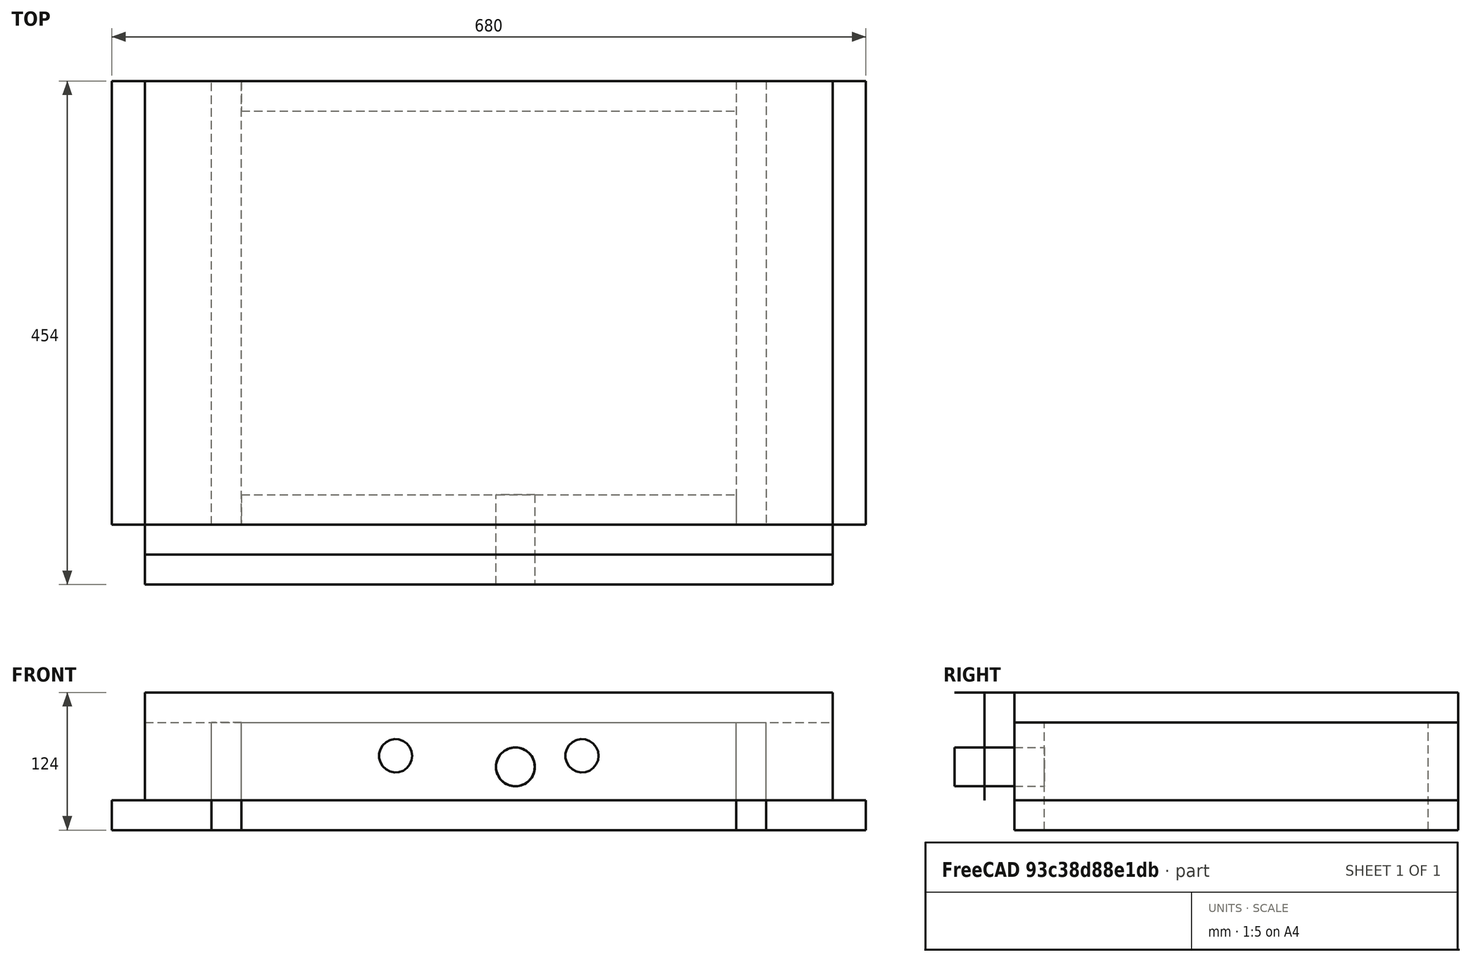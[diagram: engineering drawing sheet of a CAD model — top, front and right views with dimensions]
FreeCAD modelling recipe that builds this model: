
FCSTD DOCUMENT  (FreeCAD 0.20R25131 (Git))
Label: Werkbank
License: All rights reserved
LicenseURL: http://en.wikipedia.org/wiki/All_rights_reserved
objects: App::FeaturePython×76, Part::FeaturePython×42, App::Link×6, App::LinkElement×6
note: 41 computed .brp shape members not serialized (recipe doc carries the construction recipe); baked Part::Feature solids carry a one-line shape summary decoded from their .brp
EXTERNAL_REF file=Arbeitsfläche.FCStd obj=Assembly
EXTERNAL_REF file=Innen_hinten.FCStd obj=Assembly
EXTERNAL_REF file=Innen_vorne.FCStd obj=Assembly
EXTERNAL_REF file=Seitenteil.FCStd obj=Assembly
EXTERNAL_REF file=Grunddaten.FCStd obj=Spreadsheet
EXTERNAL_REF file=Zange.FCStd obj=Assembly
EXTERNAL_REF file=Klemmfläche.FCStd obj=Assembly

FEATURE [App::Link] Link  label="Arbeitsfläche"
  LinkedObject = -> <external Arbeitsfläche.FCStd>#Assembly
FEATURE [App::Link] Link001  label="Innen_hinten"
  LinkPlacement = pos=(87,400,-97) rot=(1,0,0;1.5708rad)
  LinkedObject = -> <external Innen_hinten.FCStd>#Assembly
  Placement = pos=(87,400,-97) rot=(1,0,0;1.5708rad)
FEATURE [App::Link] Link002  label="Innen_vorne"
  LinkPlacement = pos=(310,27,-97) rot=(1,0,0;1.5708rad)
  LinkedObject = -> <external Innen_vorne.FCStd>#Assembly
  Placement = pos=(310,27,-97) rot=(1,0,0;1.5708rad)
FEATURE [App::LinkElement] Link003_i0
  LinkPlacement = pos=(87,-4.17804e-09,-97) rot=(0,-1,0;1.5708rad)
  LinkedObject = -> <external Seitenteil.FCStd>#Assembly
  Placement = pos=(87,-4.17804e-09,-97) rot=(0,-1,0;1.5708rad)
FEATURE [App::LinkElement] Link003_i1
  LinkPlacement = pos=(533,400,-97) rot=(0.707107,0,0.707107;3.14159rad)
  LinkedObject = -> <external Seitenteil.FCStd>#Assembly
  Placement = pos=(533,400,-97) rot=(0.707107,0,0.707107;3.14159rad)
FEATURE [App::Link] Link003  label="Seitenteil"
  ElementCount = 2
  ElementList = -> [Link003_i0,Link003_i1]
  LinkedObject = -> <external Seitenteil.FCStd>#Assembly
FEATURE [App::LinkElement] Link004_i0
  LinkPlacement = pos=(310,1.40084e-11,-70) rot=(1,0,0;1.5708rad)
  LinkedObject = -> <external Zange.FCStd>#Assembly
  Placement = pos=(310,1.40084e-11,-70) rot=(1,0,0;1.5708rad)
FEATURE [App::LinkElement] Link004_i1
  LinkPlacement = pos=(310,-27,-70) rot=(1,0,0;1.5708rad)
  LinkedObject = -> <external Zange.FCStd>#Assembly
  Placement = pos=(310,-27,-70) rot=(1,0,0;1.5708rad)
FEATURE [App::Link] Link004  label="Zange"
  ElementCount = 2
  ElementList = -> [Link004_i0,Link004_i1]
  LinkedObject = -> <external Zange.FCStd>#Assembly
FEATURE [App::LinkElement] Link005_i0
  LinkPlacement = pos=(-30,9.2e-15,-97) rot=(0,0,1;0rad)
  LinkedObject = -> <external Klemmfläche.FCStd>#Assembly
  Placement = pos=(-30,9.2e-15,-97) rot=(0,0,1;0rad)
FEATURE [App::LinkElement] Link005_i1
  LinkPlacement = pos=(560,3.808e-13,-97) rot=(0,0,1;0rad)
  LinkedObject = -> <external Klemmfläche.FCStd>#Assembly
  Placement = pos=(560,3.808e-13,-97) rot=(0,0,1;0rad)
FEATURE [App::Link] Link005  label="Klemmfläche"
  ElementCount = 2
  ElementList = -> [Link005_i0,Link005_i1]
  LinkedObject = -> <external Klemmfläche.FCStd>#Assembly
FEATURE [Part::FeaturePython] Parts  # WARN: FeaturePython — macro-defined, semantics opaque (R4)
  Group = -> [Link,Link001,Link002,Link003,Link004,Link005]
  GroupMode = 0
FEATURE [Part::FeaturePython] Assembly  # WARN: FeaturePython — macro-defined, semantics opaque (R4)
  AutoRelax = true
  BuildShape = 0
  Freeze = false
  Group = -> [Constraints,Elements,Parts]
  Verbose = false
  _SolverType = 1
  _Version = 1
FEATURE [App::FeaturePython] Constraints  # WARN: FeaturePython — macro-defined, semantics opaque (R4)
  Group = -> [Constraint,Constraint001,Constraint002,Constraint003,Constraint004,Constraint005,Constraint006,Constraint007,Constraint008,Constraint009,Constraint010,Constraint013,Constraint014,Constraint015,Constraint016,Constraint017,Constraint018,Constraint019,Constraint020,Constraint021,Constraint022,Constraint023,Constraint024,Constraint025,Constraint026]
  _Version = 1
FEATURE [App::FeaturePython] Elements  # WARN: FeaturePython — macro-defined, semantics opaque (R4)
  Group = -> [_Element,_Element001,_Element002,_Element003,_Element004,_Element005,_Element006,_Element007,_Element008,_Element009,_Element010,_Element012,_Element013,_Element014,_Element015,_Element016,_Element017,_Element020,_Element022,_Element023,_Element024,_Element027,_Element028,_Element029,_Element030,_Element031,_Element032,_Element033,_Element034,_Element035,_Element036,_Element037,_Element038,+7 more]
FEATURE [App::FeaturePython] Constraint  label="Locked"  # WARN: FeaturePython — macro-defined, semantics opaque (R4)
  Disabled = false
  Group = -> [ElementLink]
  _ConstraintType = 0
  _Parent = -> Constraints
FEATURE [App::FeaturePython] ElementLink  label="Unten@Arbeitsfläche"  # link proxy (typed FeaturePython)
  LinkTransform = true
  LinkedObject = -> _Element
  _Parent = -> Constraint
FEATURE [Part::FeaturePython] _Element  label="Unten@Arbeitsfläche"  # link proxy (typed FeaturePython)
  Detach = false
  LinkTransform = true
  LinkedObject = -> Link [1.$Unten.]
  _Parent = -> Elements
FEATURE [Part::FeaturePython] _Element001  label="Oben@Innen_hinten"  # link proxy (typed FeaturePython)
  Detach = false
  LinkTransform = true
  LinkedObject = -> Link001 [1.$Oben.]
  _Parent = -> Elements
FEATURE [App::FeaturePython] Constraint001  label="PlaneAlignment"  # WARN: FeaturePython — macro-defined, semantics opaque (R4)
  Angle = 0
  AnglePitch = 0
  AngleRoll = 0
  Cascade = false
  Disabled = false
  Group = -> [ElementLink001,ElementLink002]
  LockAngle = false
  _ConstraintType = 37
  _Parent = -> Constraints
FEATURE [App::FeaturePython] ElementLink001  label="Oben@Innen_hinten"  # link proxy (typed FeaturePython)
  LinkTransform = true
  LinkedObject = -> _Element001
  _Parent = -> Constraint001
FEATURE [App::FeaturePython] ElementLink002  label="Unten@Arbeitsfläche"  # link proxy (typed FeaturePython)
  LinkTransform = true
  LinkedObject = -> _Element
  _Parent = -> Constraint001
FEATURE [App::FeaturePython] Constraint002  label="PlaneAlignment001"  # WARN: FeaturePython — macro-defined, semantics opaque (R4)
  Angle = 0
  AnglePitch = 0
  AngleRoll = 0
  Cascade = false
  Disabled = false
  Group = -> [ElementLink003,ElementLink004]
  LockAngle = false
  _ConstraintType = 37
  _Parent = -> Constraints
FEATURE [App::FeaturePython] ElementLink003  label="Hinten@Arbeitsfläche"  # link proxy (typed FeaturePython)
  LinkTransform = true
  LinkedObject = -> _Element002
  _Parent = -> Constraint002
FEATURE [Part::FeaturePython] _Element002  label="Hinten@Arbeitsfläche"  # link proxy (typed FeaturePython)
  Detach = false
  LinkTransform = true
  LinkedObject = -> Link [1.$Hinten.]
  _Parent = -> Elements
FEATURE [App::FeaturePython] ElementLink004  label="Hinten@Innen_hinten"  # link proxy (typed FeaturePython)
  LinkTransform = true
  LinkedObject = -> _Element003
  _Parent = -> Constraint002
FEATURE [Part::FeaturePython] _Element003  label="Hinten@Innen_hinten"  # link proxy (typed FeaturePython)
  Detach = false
  LinkTransform = true
  LinkedObject = -> Link001 [1.$Hinten.]
  _Parent = -> Elements
FEATURE [App::FeaturePython] Constraint003  label="PlaneAlignment002"  # WARN: FeaturePython — macro-defined, semantics opaque (R4)
  Angle = 0
  AnglePitch = 0
  AngleRoll = 0
  Cascade = false
  Disabled = false
  Group = -> [ElementLink005,ElementLink006]
  LockAngle = false
  _ConstraintType = 37
  _Parent = -> Constraints
FEATURE [App::FeaturePython] ElementLink005  label="Oben@Innen_vorne"  # link proxy (typed FeaturePython)
  LinkTransform = true
  LinkedObject = -> _Element004
  _Parent = -> Constraint003
FEATURE [Part::FeaturePython] _Element004  label="Oben@Innen_vorne"  # link proxy (typed FeaturePython)
  Detach = false
  LinkTransform = true
  LinkedObject = -> Link002 [1.$Oben.]
  _Parent = -> Elements
FEATURE [App::FeaturePython] ElementLink006  label="Unten@Arbeitsfläche"  # link proxy (typed FeaturePython)
  LinkTransform = true
  LinkedObject = -> _Element
  _Parent = -> Constraint003
FEATURE [App::FeaturePython] Constraint004  label="PlaneAlignment003"  # WARN: FeaturePython — macro-defined, semantics opaque (R4)
  Angle = 0
  AnglePitch = 0
  AngleRoll = 0
  Cascade = false
  Disabled = false
  Group = -> [ElementLink007,ElementLink008]
  LockAngle = false
  _ConstraintType = 37
  _Parent = -> Constraints
FEATURE [App::FeaturePython] ElementLink007  label="Vorne@Innen_vorne"  # link proxy (typed FeaturePython)
  LinkTransform = true
  LinkedObject = -> _Element005
  _Parent = -> Constraint004
FEATURE [Part::FeaturePython] _Element005  label="Vorne@Innen_vorne"  # link proxy (typed FeaturePython)
  Detach = false
  LinkTransform = true
  LinkedObject = -> Link002 [1.$Vorne.]
  _Parent = -> Elements
FEATURE [App::FeaturePython] ElementLink008  label="Vorne@Arbeitsfläche"  # link proxy (typed FeaturePython)
  LinkTransform = true
  LinkedObject = -> _Element006
  _Parent = -> Constraint004
FEATURE [Part::FeaturePython] _Element006  label="Vorne@Arbeitsfläche"  # link proxy (typed FeaturePython)
  Detach = false
  LinkTransform = true
  LinkedObject = -> Link [1.$Vorne.]
  _Parent = -> Elements
FEATURE [App::FeaturePython] Constraint005  label="PlaneAlignment004"  # WARN: FeaturePython — macro-defined, semantics opaque (R4)
  Angle = 0
  AnglePitch = 0
  AngleRoll = 0
  Cascade = false
  Disabled = false
  Group = -> [ElementLink009,ElementLink010]
  LockAngle = false
  _ConstraintType = 37
  _Parent = -> Constraints
FEATURE [App::FeaturePython] ElementLink009  label="_Element007"  # link proxy (typed FeaturePython)
  LinkTransform = true
  LinkedObject = -> _Element007
  _Parent = -> Constraint005
FEATURE [Part::FeaturePython] _Element007  # link proxy (typed FeaturePython)
  Detach = false
  LinkTransform = true
  LinkedObject = -> Link003 [Link003_i0.1.$Vorne.]
  _Parent = -> Elements
FEATURE [App::FeaturePython] ElementLink010  label="Vorne@Arbeitsfläche"  # link proxy (typed FeaturePython)
  LinkTransform = true
  LinkedObject = -> _Element006
  _Parent = -> Constraint005
FEATURE [App::FeaturePython] Constraint006  label="PlaneAlignment005"  # WARN: FeaturePython — macro-defined, semantics opaque (R4)
  Angle = 0
  AnglePitch = 0
  AngleRoll = 0
  Cascade = false
  Disabled = false
  Group = -> [ElementLink011,ElementLink012]
  LockAngle = false
  _ConstraintType = 37
  _Parent = -> Constraints
FEATURE [App::FeaturePython] ElementLink011  label="_Element008"  # link proxy (typed FeaturePython)
  LinkTransform = true
  LinkedObject = -> _Element008
  _Parent = -> Constraint006
FEATURE [Part::FeaturePython] _Element008  # link proxy (typed FeaturePython)
  Detach = false
  LinkTransform = true
  LinkedObject = -> Link003 [Link003_i0.1.$Oben.]
  _Parent = -> Elements
FEATURE [App::FeaturePython] ElementLink012  label="Unten@Arbeitsfläche"  # link proxy (typed FeaturePython)
  LinkTransform = true
  LinkedObject = -> _Element
  _Parent = -> Constraint006
FEATURE [App::FeaturePython] Constraint007  label="PlaneAlignment006"  # WARN: FeaturePython — macro-defined, semantics opaque (R4)
  Angle = 0
  AnglePitch = 0
  AngleRoll = 0
  Cascade = false
  Disabled = false
  Group = -> [ElementLink013,ElementLink014]
  LockAngle = false
  Offset = 60
  _ConstraintType = 37
  _Parent = -> Constraints
  expr: Offset = Grunddaten#Spreadsheet.Ueberstand
FEATURE [App::FeaturePython] ElementLink013  label="_Element009"  # link proxy (typed FeaturePython)
  LinkTransform = true
  LinkedObject = -> _Element009
  _Parent = -> Constraint007
FEATURE [Part::FeaturePython] _Element009  # link proxy (typed FeaturePython)
  Detach = false
  LinkTransform = true
  LinkedObject = -> Link003 [Link003_i0.1.$Seite.]
  _Parent = -> Elements
FEATURE [App::FeaturePython] ElementLink014  label="Links@Arbeitsfläche"  # link proxy (typed FeaturePython)
  LinkTransform = true
  LinkedObject = -> _Element010
  _Parent = -> Constraint007
FEATURE [Part::FeaturePython] _Element010  label="Links@Arbeitsfläche"  # link proxy (typed FeaturePython)
  Detach = false
  LinkTransform = true
  LinkedObject = -> Link [1.$Links.]
  _Parent = -> Elements
FEATURE [Part::FeaturePython] _Element012  label="Rechts@Arbeitsfläche"  # link proxy (typed FeaturePython)
  Detach = false
  LinkTransform = true
  LinkedObject = -> Link [1.$Rechts.]
  _Parent = -> Elements
FEATURE [Part::FeaturePython] _Element013  # link proxy (typed FeaturePython)
  Detach = false
  LinkTransform = true
  LinkedObject = -> Link004 [Link004_i0.1.$Oben.]
  _Parent = -> Elements
FEATURE [Part::FeaturePython] _Element014  label="Oben@Arbeitsfläche"  # link proxy (typed FeaturePython)
  Detach = false
  LinkTransform = true
  LinkedObject = -> Link [1.$Oben.]
  _Parent = -> Elements
FEATURE [App::FeaturePython] Constraint008  label="PlaneAlignment007"  # WARN: FeaturePython — macro-defined, semantics opaque (R4)
  Angle = 0
  AnglePitch = 0
  AngleRoll = 0
  Cascade = false
  Disabled = false
  Group = -> [ElementLink015,ElementLink016]
  LockAngle = false
  _ConstraintType = 37
  _Parent = -> Constraints
FEATURE [App::FeaturePython] ElementLink015  label="Unten@Arbeitsfläche"  # link proxy (typed FeaturePython)
  LinkTransform = true
  LinkedObject = -> _Element
  _Parent = -> Constraint008
FEATURE [App::FeaturePython] ElementLink016  label="_Element015"  # link proxy (typed FeaturePython)
  LinkTransform = true
  LinkedObject = -> _Element015
  _Parent = -> Constraint008
FEATURE [Part::FeaturePython] _Element015  # link proxy (typed FeaturePython)
  Detach = false
  LinkTransform = true
  LinkedObject = -> Link003 [Link003_i1.1.$Oben.]
  _Parent = -> Elements
FEATURE [App::FeaturePython] Constraint009  label="PlaneAlignment008"  # WARN: FeaturePython — macro-defined, semantics opaque (R4)
  Angle = 0
  AnglePitch = 0
  AngleRoll = 0
  Cascade = false
  Disabled = false
  Group = -> [ElementLink017,ElementLink018]
  LockAngle = false
  _ConstraintType = 37
  _Parent = -> Constraints
FEATURE [App::FeaturePython] ElementLink017  label="Hinten@Arbeitsfläche"  # link proxy (typed FeaturePython)
  LinkTransform = true
  LinkedObject = -> _Element002
  _Parent = -> Constraint009
FEATURE [App::FeaturePython] ElementLink018  label="_Element016"  # link proxy (typed FeaturePython)
  LinkTransform = true
  LinkedObject = -> _Element016
  _Parent = -> Constraint009
FEATURE [Part::FeaturePython] _Element016  # link proxy (typed FeaturePython)
  Detach = false
  LinkTransform = true
  LinkedObject = -> Link003 [Link003_i1.1.$Vorne.]
  _Parent = -> Elements
FEATURE [App::FeaturePython] Constraint010  label="PlaneAlignment009"  # WARN: FeaturePython — macro-defined, semantics opaque (R4)
  Angle = 0
  AnglePitch = 0
  AngleRoll = 0
  Cascade = false
  Disabled = false
  Group = -> [ElementLink019,ElementLink020]
  LockAngle = false
  Offset = 60
  _ConstraintType = 37
  _Parent = -> Constraints
  expr: Offset = Grunddaten#Spreadsheet.Ueberstand
FEATURE [App::FeaturePython] ElementLink019  label="_Element017"  # link proxy (typed FeaturePython)
  LinkTransform = true
  LinkedObject = -> _Element017
  _Parent = -> Constraint010
FEATURE [Part::FeaturePython] _Element017  # link proxy (typed FeaturePython)
  Detach = false
  LinkTransform = true
  LinkedObject = -> Link003 [Link003_i1.1.$Seite.]
  _Parent = -> Elements
FEATURE [App::FeaturePython] ElementLink020  label="Rechts@Arbeitsfläche"  # link proxy (typed FeaturePython)
  LinkTransform = true
  LinkedObject = -> _Element012
  _Parent = -> Constraint010
FEATURE [Part::FeaturePython] _Element020  # link proxy (typed FeaturePython)
  Detach = false
  LinkTransform = true
  LinkedObject = -> Link004 [1.1.$Spindel.]
  _Parent = -> Elements
FEATURE [Part::FeaturePython] _Element022  # link proxy (typed FeaturePython)
  Detach = false
  LinkTransform = true
  LinkedObject = -> Link004 [0.1.$Spindel.]
  _Parent = -> Elements
FEATURE [Part::FeaturePython] _Element023  # link proxy (typed FeaturePython)
  Detach = false
  LinkTransform = true
  LinkedObject = -> Link002 [1.$Element003.]
  _Parent = -> Elements
FEATURE [App::FeaturePython] Constraint013  label="PlaneAlignment010"  # WARN: FeaturePython — macro-defined, semantics opaque (R4)
  Angle = 0
  AnglePitch = 0
  AngleRoll = 0
  Cascade = false
  Disabled = false
  Group = -> [ElementLink025,ElementLink026]
  LockAngle = false
  _ConstraintType = 37
  _Parent = -> Constraints
FEATURE [App::FeaturePython] ElementLink025  label="_Element024"  # link proxy (typed FeaturePython)
  LinkTransform = true
  LinkedObject = -> _Element024
  _Parent = -> Constraint013
FEATURE [Part::FeaturePython] _Element024  # link proxy (typed FeaturePython)
  Detach = false
  LinkTransform = true
  LinkedObject = -> Link004 [Link004_i0.1.$Hinten.]
  _Parent = -> Elements
FEATURE [App::FeaturePython] ElementLink026  label="Vorne@Arbeitsfläche"  # link proxy (typed FeaturePython)
  LinkTransform = true
  LinkedObject = -> _Element006
  _Parent = -> Constraint013
FEATURE [App::FeaturePython] Constraint014  label="PlaneAlignment011"  # WARN: FeaturePython — macro-defined, semantics opaque (R4)
  Angle = 0
  AnglePitch = 0
  AngleRoll = 0
  Cascade = false
  Disabled = false
  Group = -> [ElementLink027,ElementLink028]
  LockAngle = false
  _ConstraintType = 37
  _Parent = -> Constraints
FEATURE [App::FeaturePython] ElementLink027  label="_Element013"  # link proxy (typed FeaturePython)
  LinkTransform = true
  LinkedObject = -> _Element013
  _Parent = -> Constraint014
FEATURE [App::FeaturePython] ElementLink028  label="Oben@Arbeitsfläche"  # link proxy (typed FeaturePython)
  LinkTransform = true
  LinkedObject = -> _Element014
  _Parent = -> Constraint014
FEATURE [Part::FeaturePython] _Element027  # link proxy (typed FeaturePython)
  Detach = false
  LinkTransform = true
  LinkedObject = -> Link004 [Link004_i0.1.$Vorne.]
  _Parent = -> Elements
FEATURE [App::FeaturePython] Constraint015  label="PlaneAlignment012"  # WARN: FeaturePython — macro-defined, semantics opaque (R4)
  Angle = 0
  AnglePitch = 0
  AngleRoll = 0
  Cascade = false
  Disabled = false
  Group = -> [ElementLink029,ElementLink030]
  LockAngle = false
  _ConstraintType = 37
  _Parent = -> Constraints
FEATURE [App::FeaturePython] ElementLink029  label="_Element028"  # link proxy (typed FeaturePython)
  LinkTransform = true
  LinkedObject = -> _Element028
  _Parent = -> Constraint015
FEATURE [Part::FeaturePython] _Element028  # link proxy (typed FeaturePython)
  Detach = false
  LinkTransform = true
  LinkedObject = -> Link002 [1.$Element004.]
  _Parent = -> Elements
FEATURE [App::FeaturePython] ElementLink030  label="_Element029"  # link proxy (typed FeaturePython)
  LinkTransform = true
  LinkedObject = -> _Element029
  _Parent = -> Constraint015
FEATURE [Part::FeaturePython] _Element029  # link proxy (typed FeaturePython)
  Detach = false
  LinkTransform = true
  LinkedObject = -> Link003 [0.1.$Element003.]
  _Parent = -> Elements
FEATURE [App::FeaturePython] Constraint016  label="PlaneAlignment013"  # WARN: FeaturePython — macro-defined, semantics opaque (R4)
  Angle = 0
  AnglePitch = 0
  AngleRoll = 0
  Cascade = false
  Disabled = false
  Group = -> [ElementLink031,ElementLink032]
  LockAngle = false
  _ConstraintType = 37
  _Parent = -> Constraints
FEATURE [App::FeaturePython] ElementLink031  label="_Element030"  # link proxy (typed FeaturePython)
  LinkTransform = true
  LinkedObject = -> _Element030
  _Parent = -> Constraint016
FEATURE [Part::FeaturePython] _Element030  # link proxy (typed FeaturePython)
  Detach = false
  LinkTransform = true
  LinkedObject = -> Link001 [1.$Element002.]
  _Parent = -> Elements
FEATURE [App::FeaturePython] ElementLink032  label="_Element029"  # link proxy (typed FeaturePython)
  LinkTransform = true
  LinkedObject = -> _Element029
  _Parent = -> Constraint016
FEATURE [App::FeaturePython] Constraint017  label="AxialAlignment"  # WARN: FeaturePython — macro-defined, semantics opaque (R4)
  Angle = 0
  AnglePitch = 0
  AngleRoll = 0
  Disabled = false
  Group = -> [ElementLink033,ElementLink034]
  LockAngle = false
  Multiply = false
  _ConstraintType = 36
  _Parent = -> Constraints
FEATURE [App::FeaturePython] ElementLink033  label="_Element031"  # link proxy (typed FeaturePython)
  LinkTransform = true
  LinkedObject = -> _Element031
  _Parent = -> Constraint017
FEATURE [Part::FeaturePython] _Element031  # link proxy (typed FeaturePython)
  Detach = false
  LinkTransform = true
  LinkedObject = -> Link004 [Link004_i0.1.$Spindel.]
  _Parent = -> Elements
FEATURE [App::FeaturePython] ElementLink034  label="Spindel@Innen_vorne"  # link proxy (typed FeaturePython)
  LinkTransform = true
  LinkedObject = -> _Element032
  _Parent = -> Constraint017
FEATURE [Part::FeaturePython] _Element032  label="Spindel@Innen_vorne"  # link proxy (typed FeaturePython)
  Detach = false
  LinkTransform = true
  LinkedObject = -> Link002 [1.$Spindel.]
  _Parent = -> Elements
FEATURE [App::FeaturePython] Constraint018  label="AxialAlignment001"  # WARN: FeaturePython — macro-defined, semantics opaque (R4)
  Angle = 0
  AnglePitch = 0
  AngleRoll = 0
  Disabled = false
  Group = -> [ElementLink035,ElementLink036]
  LockAngle = false
  Multiply = false
  _ConstraintType = 36
  _Parent = -> Constraints
FEATURE [App::FeaturePython] ElementLink035  label="_Element033"  # link proxy (typed FeaturePython)
  LinkTransform = true
  LinkedObject = -> _Element033
  _Parent = -> Constraint018
FEATURE [Part::FeaturePython] _Element033  # link proxy (typed FeaturePython)
  Detach = false
  LinkTransform = true
  LinkedObject = -> Link004 [Link004_i1.1.$Spindel.]
  _Parent = -> Elements
FEATURE [App::FeaturePython] ElementLink036  label="_Element031"  # link proxy (typed FeaturePython)
  LinkTransform = true
  LinkedObject = -> _Element031
  _Parent = -> Constraint018
FEATURE [App::FeaturePython] Constraint019  label="PlaneAlignment014"  # WARN: FeaturePython — macro-defined, semantics opaque (R4)
  Angle = 0
  AnglePitch = 0
  AngleRoll = 0
  Cascade = false
  Disabled = false
  Group = -> [ElementLink037,ElementLink038]
  LockAngle = false
  _ConstraintType = 37
  _Parent = -> Constraints
FEATURE [App::FeaturePython] ElementLink037  label="_Element013"  # link proxy (typed FeaturePython)
  LinkTransform = true
  LinkedObject = -> _Element013
  _Parent = -> Constraint019
FEATURE [App::FeaturePython] ElementLink038  label="_Element034"  # link proxy (typed FeaturePython)
  LinkTransform = true
  LinkedObject = -> _Element034
  _Parent = -> Constraint019
FEATURE [Part::FeaturePython] _Element034  # link proxy (typed FeaturePython)
  Detach = false
  LinkTransform = true
  LinkedObject = -> Link004 [Link004_i1.1.$Oben.]
  _Parent = -> Elements
FEATURE [App::FeaturePython] Constraint020  label="PlaneAlignment015"  # WARN: FeaturePython — macro-defined, semantics opaque (R4)
  Angle = 0
  AnglePitch = 0
  AngleRoll = 0
  Cascade = false
  Disabled = false
  Group = -> [ElementLink039,ElementLink040]
  LockAngle = false
  _ConstraintType = 37
  _Parent = -> Constraints
FEATURE [App::FeaturePython] ElementLink039  label="_Element007"  # link proxy (typed FeaturePython)
  LinkTransform = true
  LinkedObject = -> _Element007
  _Parent = -> Constraint020
FEATURE [App::FeaturePython] ElementLink040  label="_Element035"  # link proxy (typed FeaturePython)
  LinkTransform = true
  LinkedObject = -> _Element035
  _Parent = -> Constraint020
FEATURE [Part::FeaturePython] _Element035  # link proxy (typed FeaturePython)
  Detach = false
  LinkTransform = true
  LinkedObject = -> Link005 [Link005_i0.1.$Vorne.]
  _Parent = -> Elements
FEATURE [App::FeaturePython] Constraint021  label="PlaneAlignment016"  # WARN: FeaturePython — macro-defined, semantics opaque (R4)
  Angle = 0
  AnglePitch = 0
  AngleRoll = 0
  Cascade = false
  Disabled = false
  Group = -> [ElementLink041,ElementLink042]
  LockAngle = false
  _ConstraintType = 37
  _Parent = -> Constraints
FEATURE [App::FeaturePython] ElementLink041  label="_Element036"  # link proxy (typed FeaturePython)
  LinkTransform = true
  LinkedObject = -> _Element036
  _Parent = -> Constraint021
FEATURE [Part::FeaturePython] _Element036  # link proxy (typed FeaturePython)
  Detach = false
  LinkTransform = true
  LinkedObject = -> Link005 [Link005_i0.1.$Rechts.]
  _Parent = -> Elements
FEATURE [App::FeaturePython] ElementLink042  label="_Element009"  # link proxy (typed FeaturePython)
  LinkTransform = true
  LinkedObject = -> _Element009
  _Parent = -> Constraint021
FEATURE [App::FeaturePython] Constraint022  label="PlaneAlignment017"  # WARN: FeaturePython — macro-defined, semantics opaque (R4)
  Angle = 0
  AnglePitch = 0
  AngleRoll = 0
  Cascade = false
  Disabled = false
  Group = -> [ElementLink043,ElementLink044]
  LockAngle = false
  _ConstraintType = 37
  _Parent = -> Constraints
FEATURE [App::FeaturePython] ElementLink043  label="_Element037"  # link proxy (typed FeaturePython)
  LinkTransform = true
  LinkedObject = -> _Element037
  _Parent = -> Constraint022
FEATURE [Part::FeaturePython] _Element037  # link proxy (typed FeaturePython)
  Detach = false
  LinkTransform = true
  LinkedObject = -> Link005 [Link005_i1.1.$Vorne.]
  _Parent = -> Elements
FEATURE [App::FeaturePython] ElementLink044  label="_Element007"  # link proxy (typed FeaturePython)
  LinkTransform = true
  LinkedObject = -> _Element007
  _Parent = -> Constraint022
FEATURE [Part::FeaturePython] _Element038  # link proxy (typed FeaturePython)
  Detach = false
  LinkTransform = true
  LinkedObject = -> Link005 [Link005_i0.1.$Links.]
  _Parent = -> Elements
FEATURE [App::FeaturePython] Constraint023  label="PlaneAlignment018"  # WARN: FeaturePython — macro-defined, semantics opaque (R4)
  Angle = 0
  AnglePitch = 0
  AngleRoll = 0
  Cascade = false
  Disabled = false
  Group = -> [ElementLink045,ElementLink046]
  LockAngle = false
  _ConstraintType = 37
  _Parent = -> Constraints
FEATURE [App::FeaturePython] ElementLink045  label="_Element039"  # link proxy (typed FeaturePython)
  LinkTransform = true
  LinkedObject = -> _Element039
  _Parent = -> Constraint023
FEATURE [Part::FeaturePython] _Element039  # link proxy (typed FeaturePython)
  Detach = false
  LinkTransform = true
  LinkedObject = -> Link005 [0.1.$Unten.]
  _Parent = -> Elements
FEATURE [App::FeaturePython] ElementLink046  label="_Element040"  # link proxy (typed FeaturePython)
  LinkTransform = true
  LinkedObject = -> _Element040
  _Parent = -> Constraint023
FEATURE [Part::FeaturePython] _Element040  # link proxy (typed FeaturePython)
  Detach = false
  LinkTransform = true
  LinkedObject = -> Link003 [0.1.$Element004.]
  _Parent = -> Elements
FEATURE [App::FeaturePython] Constraint024  label="PlaneAlignment019"  # WARN: FeaturePython — macro-defined, semantics opaque (R4)
  Angle = 0
  AnglePitch = 0
  AngleRoll = 0
  Cascade = false
  Disabled = false
  Group = -> [ElementLink047,ElementLink048]
  LockAngle = false
  _ConstraintType = 37
  _Parent = -> Constraints
FEATURE [App::FeaturePython] ElementLink047  label="_Element041"  # link proxy (typed FeaturePython)
  LinkTransform = true
  LinkedObject = -> _Element041
  _Parent = -> Constraint024
FEATURE [Part::FeaturePython] _Element041  # link proxy (typed FeaturePython)
  Detach = false
  LinkTransform = true
  LinkedObject = -> Link005 [Link005_i1.1.$Unten.]
  _Parent = -> Elements
FEATURE [App::FeaturePython] ElementLink048  label="_Element042"  # link proxy (typed FeaturePython)
  LinkTransform = true
  LinkedObject = -> _Element042
  _Parent = -> Constraint024
FEATURE [Part::FeaturePython] _Element042  # link proxy (typed FeaturePython)
  Detach = false
  LinkTransform = true
  LinkedObject = -> Link005 [Link005_i0.1.$Unten.]
  _Parent = -> Elements
FEATURE [App::FeaturePython] Constraint025  label="PlaneAlignment020"  # WARN: FeaturePython — macro-defined, semantics opaque (R4)
  Angle = 0
  AnglePitch = 0
  AngleRoll = 0
  Cascade = false
  Disabled = false
  Group = -> [ElementLink049,ElementLink050]
  LockAngle = false
  _ConstraintType = 37
  _Parent = -> Constraints
FEATURE [App::FeaturePython] ElementLink049  label="_Element043"  # link proxy (typed FeaturePython)
  LinkTransform = true
  LinkedObject = -> _Element043
  _Parent = -> Constraint025
FEATURE [Part::FeaturePython] _Element043  # link proxy (typed FeaturePython)
  Detach = false
  LinkTransform = true
  LinkedObject = -> Link005 [Link005_i1.1.$Links.]
  _Parent = -> Elements
FEATURE [App::FeaturePython] ElementLink050  label="_Element017"  # link proxy (typed FeaturePython)
  LinkTransform = true
  LinkedObject = -> _Element017
  _Parent = -> Constraint025
FEATURE [App::FeaturePython] Constraint026  label="PlaneAlignment021"  # WARN: FeaturePython — macro-defined, semantics opaque (R4)
  Angle = 0
  AnglePitch = 0
  AngleRoll = 0
  Cascade = false
  Disabled = false
  Group = -> [ElementLink051,ElementLink052]
  LockAngle = false
  _ConstraintType = 37
  _Parent = -> Constraints
FEATURE [App::FeaturePython] ElementLink051  label="_Element044"  # link proxy (typed FeaturePython)
  LinkTransform = true
  LinkedObject = -> _Element044
  _Parent = -> Constraint026
FEATURE [Part::FeaturePython] _Element044  # link proxy (typed FeaturePython)
  Detach = false
  LinkTransform = true
  LinkedObject = -> Link004 [1.1.$Hinten.]
  _Parent = -> Elements
FEATURE [App::FeaturePython] ElementLink052  label="_Element045"  # link proxy (typed FeaturePython)
  LinkTransform = true
  LinkedObject = -> _Element045
  _Parent = -> Constraint026
FEATURE [Part::FeaturePython] _Element045  # link proxy (typed FeaturePython)
  Detach = false
  LinkTransform = true
  LinkedObject = -> Link004 [0.1.$Vorne.]
  _Parent = -> Elements

RESOLVED EXTERNAL PARTS (link-assembly join: the EXTERNAL_REF files above that resolve inside this repo's crawl, each included once):
---- part Arbeitsfläche.FCStd = doc fcstd_90bbc381280e ----
FCSTD DOCUMENT  (FreeCAD 0.20R25131 (Git))
Label: Arbeitsfläche
License: All rights reserved
LicenseURL: http://en.wikipedia.org/wiki/All_rights_reserved
objects: Part::FeaturePython×8, App::FeaturePython×2, Part::Box×1, Part::Cylinder×1, Part::Cut×1
note: 10 computed .brp shape members not serialized (recipe doc carries the construction recipe); baked Part::Feature solids carry a one-line shape summary decoded from their .brp
EXTERNAL_REF file=Grunddaten.FCStd obj=Spreadsheet

FEATURE [Part::Box] Box  label="Cube"
  AttacherType = Attacher::AttachEngine3D
  Height = 27
  Length = 620
  Width = 400
  expr: Length = <<Grunddaten>>#Spreadsheet.Arbeitsflaeche + 2 * <<Grunddaten>>#Spreadsheet.Ueberstand
  expr: Width = <<Grunddaten>>#Spreadsheet.Plattenbreite
  expr: Height = <<Grunddaten>>#Spreadsheet.Plattendicke
FEATURE [App::FeaturePython] Constraints  # WARN: FeaturePython — macro-defined, semantics opaque (R4)
  _Version = 1
FEATURE [Part::Cylinder] Cylinder  label="Schraubzwinge_oben"
  Angle = 360
  AttacherType = Attacher::AttachEngine3D
  FirstAngle = 0
  Height = 30
  Placement = pos=(485,60,0) rot=(0,0,1;0rad)
  Radius = 25
  SecondAngle = 0
  expr: .Placement.Base.x = Grunddaten#Spreadsheet.Arbeitsflaeche + Grunddaten#Spreadsheet.Ueberstand - 75mm
FEATURE [Part::Cut] Cut
  Base = -> Box
  Tool = -> Cylinder
FEATURE [Part::FeaturePython] Parts  # WARN: FeaturePython — macro-defined, semantics opaque (R4)
  Group = -> [Box,Cylinder,Cut]
  GroupMode = 0
FEATURE [Part::FeaturePython] Assembly  label="Arbeitsfläche"  # WARN: FeaturePython — macro-defined, semantics opaque (R4)
  AutoRelax = true
  BuildShape = 0
  Freeze = false
  Group = -> [Constraints,Elements,Parts]
  Verbose = false
  _SolverType = 1
  _Version = 1
FEATURE [App::FeaturePython] Elements  # WARN: FeaturePython — macro-defined, semantics opaque (R4)
  Group = -> [Element,Element001,Element002,Element003,Element004,Element005]
FEATURE [Part::FeaturePython] Element  label="Unten"  # link proxy (typed FeaturePython)
  Detach = false
  LinkTransform = true
  LinkedObject = -> Box [Face5]
  _Parent = -> Elements
FEATURE [Part::FeaturePython] Element001  label="Vorne"  # link proxy (typed FeaturePython)
  Detach = false
  LinkTransform = true
  LinkedObject = -> Box [Face3]
  _Parent = -> Elements
FEATURE [Part::FeaturePython] Element002  label="Hinten"  # link proxy (typed FeaturePython)
  Detach = false
  LinkTransform = true
  LinkedObject = -> Box [Face4]
  _Parent = -> Elements
FEATURE [Part::FeaturePython] Element003  label="Rechts"  # link proxy (typed FeaturePython)
  Detach = false
  LinkTransform = true
  LinkedObject = -> Box [Face2]
  _Parent = -> Elements
FEATURE [Part::FeaturePython] Element004  label="Links"  # link proxy (typed FeaturePython)
  Detach = false
  LinkTransform = true
  LinkedObject = -> Box [Face1]
  _Parent = -> Elements
FEATURE [Part::FeaturePython] Element005  label="Oben"  # link proxy (typed FeaturePython)
  Detach = false
  LinkTransform = true
  LinkedObject = -> Box [Face6]
  _Parent = -> Elements
---- part Grunddaten.FCStd = doc fcstd_a2668720d712 ----
FCSTD DOCUMENT  (FreeCAD 0.20R25131 (Git))
Label: Grunddaten
License: All rights reserved
LicenseURL: http://en.wikipedia.org/wiki/All_rights_reserved
objects: Spreadsheet::Sheet×1

FEATURE [Spreadsheet::Sheet] Spreadsheet
  cells = A2=Plattendicke; B2(Plattendicke)==27mm; A3=Plattenbreite; B3(Plattenbreite)==400mm; A4=Arbeitsflaeche; B4(Arbeitsflaeche)==500mm; A5=Hoehe; B5(Hoehe)==97mm; A6=Klemmflaeche; B6(Klemmflaeche)==90mm; A7=Innenmass; B7(Innenmass)==B4 - 2 * B2; A8=Ueberstand; B8(Ueberstand)==60mm; C9=Diese Werte sind nach dem Foto geschätzt!; A10=Spindel_Links; B10(Spindel_Links)==84mm; A11=Spindel_Rechts; B11(Spindel_Rechts)==84mm; A12=Spindel_Hoehe; B12(Spindel_Hoehe)==30mm; C12=im eingebautem Zustand von open; A13=Spindel_Antrieb; B13(Spindel_Antrieb)==24mm; A14=Spindel_Antrieb_Hoehe; B14(Spindel_Antrieb_Hoehe)==40mm; C14=im eingebautem Zustand von oben
---- part Innen_hinten.FCStd = doc fcstd_743176cbf1e2 ----
FCSTD DOCUMENT  (FreeCAD 0.20R25131 (Git))
Label: Innen_hinten
License: All rights reserved
LicenseURL: http://en.wikipedia.org/wiki/All_rights_reserved
objects: Part::FeaturePython×8, App::FeaturePython×2, Part::Box×1
note: 8 computed .brp shape members not serialized (recipe doc carries the construction recipe); baked Part::Feature solids carry a one-line shape summary decoded from their .brp
EXTERNAL_REF file=Grunddaten.FCStd obj=Spreadsheet

FEATURE [Part::Box] Box  label="Cube"
  AttacherType = Attacher::AttachEngine3D
  Height = 27
  Length = 446
  Width = 97
  expr: Length = <<Grunddaten>>#Spreadsheet.Innenmass
  expr: Width = <<Grunddaten>>#Spreadsheet.Hoehe
  expr: Height = <<Grunddaten>>#Spreadsheet.Plattendicke
FEATURE [App::FeaturePython] Constraints  # WARN: FeaturePython — macro-defined, semantics opaque (R4)
  _Version = 1
FEATURE [Part::FeaturePython] Parts  # WARN: FeaturePython — macro-defined, semantics opaque (R4)
  Group = -> [Box]
  GroupMode = 0
FEATURE [Part::FeaturePython] Assembly  label="Innen_hinten"  # WARN: FeaturePython — macro-defined, semantics opaque (R4)
  AutoRelax = true
  BuildShape = 0
  Freeze = false
  Group = -> [Constraints,Elements,Parts]
  Verbose = false
  _SolverType = 1
  _Version = 1
FEATURE [App::FeaturePython] Elements  # WARN: FeaturePython — macro-defined, semantics opaque (R4)
  Group = -> [Element,Element001,Element002,Element003,Element004,Element005]
FEATURE [Part::FeaturePython] Element  label="Oben"  # link proxy (typed FeaturePython)
  Detach = false
  LinkTransform = true
  LinkedObject = -> Box [Face4]
  _Parent = -> Elements
FEATURE [Part::FeaturePython] Element001  label="Hinten"  # link proxy (typed FeaturePython)
  Detach = false
  LinkTransform = true
  LinkedObject = -> Box [Face5]
  _Parent = -> Elements
FEATURE [Part::FeaturePython] Element002  # link proxy (typed FeaturePython)
  Detach = false
  LinkTransform = true
  LinkedObject = -> Box [Face1]
  _Parent = -> Elements
FEATURE [Part::FeaturePython] Element003  # link proxy (typed FeaturePython)
  Detach = false
  LinkTransform = true
  LinkedObject = -> Box [Face6]
  _Parent = -> Elements
FEATURE [Part::FeaturePython] Element004  # link proxy (typed FeaturePython)
  Detach = false
  LinkTransform = true
  LinkedObject = -> Box [Face2]
  _Parent = -> Elements
FEATURE [Part::FeaturePython] Element005  # link proxy (typed FeaturePython)
  Detach = false
  LinkTransform = true
  LinkedObject = -> Box [Face3]
  _Parent = -> Elements
---- part Innen_vorne.FCStd = doc fcstd_2986dde7ab49 ----
FCSTD DOCUMENT  (FreeCAD 0.20R25131 (Git))
Label: Innen_vorne
License: All rights reserved
LicenseURL: http://en.wikipedia.org/wiki/All_rights_reserved
objects: Part::FeaturePython×9, Part::Cylinder×3, App::FeaturePython×2, Part::Box×1, Part::MultiFuse×1, Part::Cut×1
note: 14 computed .brp shape members not serialized (recipe doc carries the construction recipe); baked Part::Feature solids carry a one-line shape summary decoded from their .brp
EXTERNAL_REF file=Grunddaten.FCStd obj=Spreadsheet

FEATURE [Part::Box] Box  label="Cube"
  AttacherType = Attacher::AttachEngine3D
  Height = 27
  Length = 446
  Placement = pos=(-223,0,0) rot=(0,0,1;0rad)
  Width = 97
  expr: .Placement.Base.x = -Length / 2
  expr: Height = <<Grunddaten>>#Spreadsheet.Plattendicke
  expr: Width = <<Grunddaten>>#Spreadsheet.Hoehe
  expr: Length = <<Grunddaten>>#Spreadsheet.Innenmass
FEATURE [Part::Cylinder] Cylinder  label="Führung_rechts"
  Angle = 360
  AttacherType = Attacher::AttachEngine3D
  FirstAngle = 0
  Height = 30
  Placement = pos=(84,67,0) rot=(0,0,1;0rad)
  Radius = 15
  SecondAngle = 0
  expr: .Placement.Base.x = Grunddaten#Spreadsheet.Spindel_Links
  expr: .Placement.Base.y = Grunddaten#Spreadsheet.Hoehe - Grunddaten#Spreadsheet.Spindel_Hoehe
FEATURE [Part::Cylinder] Cylinder001  label="Führung_links"
  Angle = 360
  AttacherType = Attacher::AttachEngine3D
  FirstAngle = 0
  Height = 30
  Placement = pos=(-84,67,0) rot=(0,0,1;0rad)
  Radius = 15
  SecondAngle = 0
  expr: .Placement.Base.x = -Grunddaten#Spreadsheet.Spindel_Links
  expr: .Placement.Base.y = Grunddaten#Spreadsheet.Hoehe - Grunddaten#Spreadsheet.Spindel_Hoehe
FEATURE [Part::Cylinder] Cylinder002  label="Spindel"
  Angle = 360
  AttacherType = Attacher::AttachEngine3D
  FirstAngle = 0
  Height = 30
  Placement = pos=(24,57,0) rot=(0,0,1;0rad)
  Radius = 17.5
  SecondAngle = 0
  expr: .Placement.Base.y = Grunddaten#Spreadsheet.Hoehe - Grunddaten#Spreadsheet.Spindel_Antrieb_Hoehe
  expr: .Placement.Base.x = Grunddaten#Spreadsheet.Spindel_Antrieb
FEATURE [App::FeaturePython] Constraints  # WARN: FeaturePython — macro-defined, semantics opaque (R4)
  _Version = 1
FEATURE [Part::MultiFuse] Fusion
  Shapes = -> [Cylinder,Cylinder001,Cylinder002]
FEATURE [Part::Cut] Cut
  Base = -> Box
  Tool = -> Fusion
FEATURE [Part::FeaturePython] Parts  # WARN: FeaturePython — macro-defined, semantics opaque (R4)
  Group = -> [Box,Cylinder,Cylinder001,Cylinder002,Fusion,Cut]
  GroupMode = 0
FEATURE [Part::FeaturePython] Assembly  label="Innen_vorne"  # WARN: FeaturePython — macro-defined, semantics opaque (R4)
  AutoRelax = true
  BuildShape = 0
  Freeze = false
  Group = -> [Constraints,Elements,Parts]
  Verbose = false
  _SolverType = 1
  _Version = 1
FEATURE [App::FeaturePython] Elements  # WARN: FeaturePython — macro-defined, semantics opaque (R4)
  Group = -> [Element,Element001,Element002,Element003,Element004,Element005,Element006]
FEATURE [Part::FeaturePython] Element  label="Vorne"  # link proxy (typed FeaturePython)
  Detach = false
  LinkTransform = true
  LinkedObject = -> Cut [Face3]
  _Parent = -> Elements
FEATURE [Part::FeaturePython] Element001  label="Oben"  # link proxy (typed FeaturePython)
  Detach = false
  LinkTransform = true
  LinkedObject = -> Cut [Face4]
  _Parent = -> Elements
FEATURE [Part::FeaturePython] Element002  label="Spindel"  # link proxy (typed FeaturePython)
  Detach = false
  LinkTransform = true
  LinkedObject = -> Cut [Face7]
  _Parent = -> Elements
FEATURE [Part::FeaturePython] Element003  # link proxy (typed FeaturePython)
  Detach = false
  LinkTransform = true
  LinkedObject = -> Cut [Edge10]
  _Parent = -> Elements
FEATURE [Part::FeaturePython] Element004  # link proxy (typed FeaturePython)
  Detach = false
  LinkTransform = true
  LinkedObject = -> Cut [Face1]
  _Parent = -> Elements
FEATURE [Part::FeaturePython] Element005  # link proxy (typed FeaturePython)
  Detach = false
  LinkTransform = true
  LinkedObject = -> Cut [Face6]
  _Parent = -> Elements
FEATURE [Part::FeaturePython] Element006  # link proxy (typed FeaturePython)
  Detach = false
  LinkTransform = true
  LinkedObject = -> Cut [Face2]
  _Parent = -> Elements
---- part Klemmfläche.FCStd = doc fcstd_d60b58048bda ----
FCSTD DOCUMENT  (FreeCAD 0.20R25131 (Git))
Label: Klemmfläche
License: All rights reserved
LicenseURL: http://en.wikipedia.org/wiki/All_rights_reserved
objects: Part::FeaturePython×7, App::FeaturePython×2, Part::Box×1
note: 7 computed .brp shape members not serialized (recipe doc carries the construction recipe); baked Part::Feature solids carry a one-line shape summary decoded from their .brp
EXTERNAL_REF file=Grunddaten.FCStd obj=Spreadsheet

FEATURE [Part::Box] Box  label="Cube"
  AttacherType = Attacher::AttachEngine3D
  Height = 27
  Length = 90
  Width = 400
  expr: Length = <<Grunddaten>>#Spreadsheet.Klemmflaeche
  expr: Width = <<Grunddaten>>#Spreadsheet.Plattenbreite
  expr: Height = <<Grunddaten>>#Spreadsheet.Plattendicke
FEATURE [App::FeaturePython] Constraints  # WARN: FeaturePython — macro-defined, semantics opaque (R4)
  _Version = 1
FEATURE [Part::FeaturePython] Parts  # WARN: FeaturePython — macro-defined, semantics opaque (R4)
  Group = -> [Box]
  GroupMode = 0
FEATURE [Part::FeaturePython] Assembly  label="Klemmfläche"  # WARN: FeaturePython — macro-defined, semantics opaque (R4)
  AutoRelax = true
  BuildShape = 0
  Freeze = false
  Group = -> [Constraints,Elements,Parts]
  Verbose = false
  _SolverType = 1
  _Version = 1
FEATURE [App::FeaturePython] Elements  # WARN: FeaturePython — macro-defined, semantics opaque (R4)
  Group = -> [Element,Element001,Element002,Element003,Element004]
FEATURE [Part::FeaturePython] Element  label="Vorne"  # link proxy (typed FeaturePython)
  Detach = false
  LinkTransform = true
  LinkedObject = -> Box [Face3]
  _Parent = -> Elements
FEATURE [Part::FeaturePython] Element001  label="Unten"  # link proxy (typed FeaturePython)
  Detach = false
  LinkTransform = true
  LinkedObject = -> Box [Face5]
  _Parent = -> Elements
FEATURE [Part::FeaturePython] Element002  label="Rechts"  # link proxy (typed FeaturePython)
  Detach = false
  LinkTransform = true
  LinkedObject = -> Box [Face2]
  _Parent = -> Elements
FEATURE [Part::FeaturePython] Element003  label="Links"  # link proxy (typed FeaturePython)
  Detach = false
  LinkTransform = true
  LinkedObject = -> Box [Face1]
  _Parent = -> Elements
FEATURE [Part::FeaturePython] Element004  # link proxy (typed FeaturePython)
  Detach = false
  LinkTransform = true
  LinkedObject = -> Box [Face6]
  _Parent = -> Elements
---- part Seitenteil.FCStd = doc fcstd_1cb6ae5e1e0b ----
FCSTD DOCUMENT  (FreeCAD 0.20R25131 (Git))
Label: Seitenteil
License: All rights reserved
LicenseURL: http://en.wikipedia.org/wiki/All_rights_reserved
objects: Part::FeaturePython×8, Part::Box×2, App::FeaturePython×2, Part::MultiFuse×2, Part::Cylinder×1, Part::Mirroring×1, Part::Cut×1
note: 14 computed .brp shape members not serialized (recipe doc carries the construction recipe); baked Part::Feature solids carry a one-line shape summary decoded from their .brp
EXTERNAL_REF file=Grunddaten.FCStd obj=Spreadsheet

FEATURE [Part::Box] Box  label="Cube"
  AttacherType = Attacher::AttachEngine3D
  Height = 27
  Length = 97
  Width = 400
  expr: Length = <<Grunddaten>>#Spreadsheet.Hoehe
  expr: Width = <<Grunddaten>>#Spreadsheet.Plattenbreite
  expr: Height = <<Grunddaten>>#Spreadsheet.Plattendicke
FEATURE [App::FeaturePython] Constraints  # WARN: FeaturePython — macro-defined, semantics opaque (R4)
  _Version = 1
FEATURE [Part::Cylinder] Cylinder
  Angle = 360
  AttacherType = Attacher::AttachEngine3D
  FirstAngle = 0
  Height = 30
  Placement = pos=(69.5,50,0) rot=(0,0,1;0rad)
  Radius = 17.5
  SecondAngle = 0
  expr: .Placement.Base.x = <<Grunddaten>>#Spreadsheet.Hoehe - Radius - 10mm
FEATURE [Part::Box] Box001  label="Cube001"
  AttacherType = Attacher::AttachEngine3D
  Height = 30
  Length = 35
  Placement = pos=(69.5,32.5,0) rot=(0,0,1;0rad)
  Width = 35
  expr: Length = 2 * Cylinder.Radius
  expr: Width = 2 * Cylinder.Radius
  expr: .Placement.Base.x = <<Grunddaten>>#Spreadsheet.Hoehe - Length / 2 - 10mm
  expr: .Placement.Base.y = 50mm - Width / 2
FEATURE [Part::MultiFuse] Fusion
  Shapes = -> [Cylinder,Box001]
FEATURE [Part::Mirroring] Part__Mirroring  label="Fusion (Mirror #1)"
  Base = (0,200,0)
  Normal = (0,1,0)
  Source = -> Fusion
FEATURE [Part::MultiFuse] Fusion001
  Shapes = -> [Fusion,Part__Mirroring]
FEATURE [Part::Cut] Cut
  Base = -> Box
  Tool = -> Fusion001
FEATURE [Part::FeaturePython] Parts  # WARN: FeaturePython — macro-defined, semantics opaque (R4)
  Group = -> [Box,Cylinder,Box001,Fusion,Part__Mirroring,Fusion001,Cut]
  GroupMode = 0
FEATURE [Part::FeaturePython] Assembly  label="Seitenteil"  # WARN: FeaturePython — macro-defined, semantics opaque (R4)
  AutoRelax = true
  BuildShape = 0
  Freeze = false
  Group = -> [Constraints,Elements,Parts]
  Verbose = false
  _SolverType = 1
  _Version = 1
FEATURE [App::FeaturePython] Elements  # WARN: FeaturePython — macro-defined, semantics opaque (R4)
  Group = -> [Element,Element001,Element002,Element003,Element004,Element005]
FEATURE [Part::FeaturePython] Element  label="Oben"  # link proxy (typed FeaturePython)
  Detach = false
  LinkTransform = true
  LinkedObject = -> Box [Face2]
  _Parent = -> Elements
FEATURE [Part::FeaturePython] Element001  label="Seite"  # link proxy (typed FeaturePython)
  Detach = false
  LinkTransform = true
  LinkedObject = -> Box [Face6]
  _Parent = -> Elements
FEATURE [Part::FeaturePython] Element002  label="Vorne"  # link proxy (typed FeaturePython)
  Detach = false
  LinkTransform = true
  LinkedObject = -> Box [Face3]
  _Parent = -> Elements
FEATURE [Part::FeaturePython] Element003  # link proxy (typed FeaturePython)
  Detach = false
  LinkTransform = true
  LinkedObject = -> Box [Face5]
  _Parent = -> Elements
FEATURE [Part::FeaturePython] Element004  # link proxy (typed FeaturePython)
  Detach = false
  LinkTransform = true
  LinkedObject = -> Box [Face1]
  _Parent = -> Elements
FEATURE [Part::FeaturePython] Element005  # link proxy (typed FeaturePython)
  Detach = false
  LinkTransform = true
  LinkedObject = -> Box [Face4]
  _Parent = -> Elements
---- part Zange.FCStd = doc fcstd_8ed8d12e8266 ----
FCSTD DOCUMENT  (FreeCAD 0.20R25131 (Git))
Label: Zange
License: All rights reserved
LicenseURL: http://en.wikipedia.org/wiki/All_rights_reserved
objects: Part::FeaturePython×10, Part::Cylinder×3, App::FeaturePython×2, Part::Box×1, Part::MultiFuse×1, Part::Cut×1
note: 15 computed .brp shape members not serialized (recipe doc carries the construction recipe); baked Part::Feature solids carry a one-line shape summary decoded from their .brp
EXTERNAL_REF file=Grunddaten.FCStd obj=Spreadsheet

FEATURE [Part::Box] Box  label="Cube"
  AttacherType = Attacher::AttachEngine3D
  Height = 27
  Length = 620
  Placement = pos=(-310,0,0) rot=(0,0,1;0rad)
  Width = 97
  expr: .Placement.Base.x = -Length / 2
  expr: Length = <<Grunddaten>>#Spreadsheet.Arbeitsflaeche + 2 * <<Grunddaten>>#Spreadsheet.Ueberstand
  expr: Width = <<Grunddaten>>#Spreadsheet.Hoehe
  expr: Height = <<Grunddaten>>#Spreadsheet.Plattendicke
FEATURE [Part::Cylinder] Cylinder  label="Führung_rechts"
  Angle = 360
  AttacherType = Attacher::AttachEngine3D
  FirstAngle = 0
  Height = 30
  Placement = pos=(84,40,0) rot=(0,0,1;0rad)
  Radius = 15
  SecondAngle = 0
  expr: .Placement.Base.y = -Grunddaten#Spreadsheet.Plattendicke + Grunddaten#Spreadsheet.Hoehe - Grunddaten#Spreadsheet.Spindel_Hoehe
  expr: .Placement.Base.x = Grunddaten#Spreadsheet.Spindel_Links
FEATURE [Part::Cylinder] Cylinder001  label="Führung_links"
  Angle = 360
  AttacherType = Attacher::AttachEngine3D
  FirstAngle = 0
  Height = 30
  Placement = pos=(-84,40,0) rot=(0,0,1;0rad)
  Radius = 15
  SecondAngle = 0
  expr: .Placement.Base.y = -Grunddaten#Spreadsheet.Plattendicke + Grunddaten#Spreadsheet.Hoehe - Grunddaten#Spreadsheet.Spindel_Hoehe
  expr: .Placement.Base.x = -Grunddaten#Spreadsheet.Spindel_Links
FEATURE [Part::Cylinder] Cylinder002  label="Spindel"
  Angle = 360
  AttacherType = Attacher::AttachEngine3D
  FirstAngle = 0
  Height = 30
  Placement = pos=(24,30,0) rot=(0,0,1;0rad)
  Radius = 17.5
  SecondAngle = 0
  expr: .Placement.Base.x = Grunddaten#Spreadsheet.Spindel_Antrieb
  expr: .Placement.Base.y = -Grunddaten#Spreadsheet.Plattendicke + Grunddaten#Spreadsheet.Hoehe - Grunddaten#Spreadsheet.Spindel_Antrieb_Hoehe
FEATURE [App::FeaturePython] Constraints  # WARN: FeaturePython — macro-defined, semantics opaque (R4)
  _Version = 1
FEATURE [Part::MultiFuse] Fusion
  Shapes = -> [Cylinder,Cylinder001,Cylinder002]
FEATURE [Part::Cut] Cut
  Base = -> Box
  Tool = -> Fusion
FEATURE [Part::FeaturePython] Parts  # WARN: FeaturePython — macro-defined, semantics opaque (R4)
  Group = -> [Box,Cylinder,Cylinder001,Cylinder002,Fusion,Cut]
  GroupMode = 0
FEATURE [Part::FeaturePython] Assembly  label="Zange"  # WARN: FeaturePython — macro-defined, semantics opaque (R4)
  AutoRelax = true
  BuildShape = 0
  Freeze = false
  Group = -> [Constraints,Elements,Parts]
  Verbose = false
  _SolverType = 1
  _Version = 1
FEATURE [App::FeaturePython] Elements  # WARN: FeaturePython — macro-defined, semantics opaque (R4)
  Group = -> [Element,Element001,Element002,Element003,Element004,Element005,Element006,Element007]
FEATURE [Part::FeaturePython] Element  label="Vorne"  # link proxy (typed FeaturePython)
  Detach = false
  LinkTransform = true
  LinkedObject = -> Cut [Face3]
  _Parent = -> Elements
FEATURE [Part::FeaturePython] Element001  label="Oben"  # link proxy (typed FeaturePython)
  Detach = false
  LinkTransform = true
  LinkedObject = -> Cut [Face4]
  _Parent = -> Elements
FEATURE [Part::FeaturePython] Element002  label="Spindel"  # link proxy (typed FeaturePython)
  Detach = false
  LinkTransform = true
  LinkedObject = -> Cut [Face7]
  _Parent = -> Elements
FEATURE [Part::FeaturePython] Element003  label="Hinten"  # link proxy (typed FeaturePython)
  Detach = false
  LinkTransform = true
  LinkedObject = -> Cut [Face5]
  _Parent = -> Elements
FEATURE [Part::FeaturePython] Element004  # link proxy (typed FeaturePython)
  Detach = false
  LinkTransform = true
  LinkedObject = -> Cut [Edge10]
  _Parent = -> Elements
FEATURE [Part::FeaturePython] Element005  # link proxy (typed FeaturePython)
  Detach = false
  LinkTransform = true
  LinkedObject = -> Cut [Face6]
  _Parent = -> Elements
FEATURE [Part::FeaturePython] Element006  # link proxy (typed FeaturePython)
  Detach = false
  LinkTransform = true
  LinkedObject = -> Cut [Face2]
  _Parent = -> Elements
FEATURE [Part::FeaturePython] Element007  # link proxy (typed FeaturePython)
  Detach = false
  LinkTransform = true
  LinkedObject = -> Cut [Face1]
  _Parent = -> Elements
